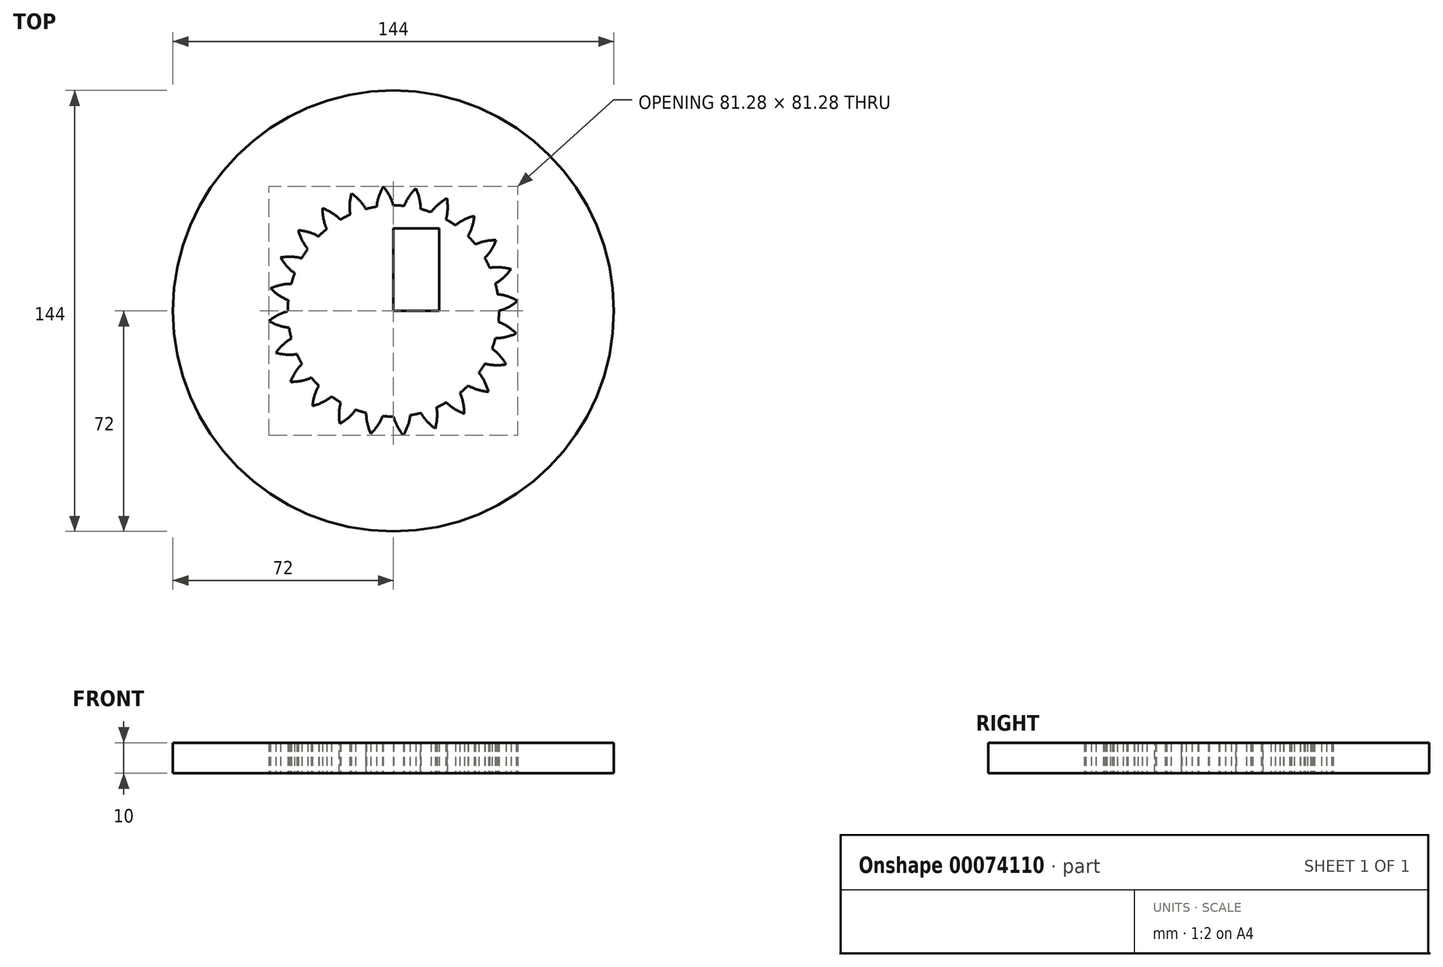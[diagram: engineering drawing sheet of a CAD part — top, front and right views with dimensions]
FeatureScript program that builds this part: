
annotation { "Feature Type Name" : "Feature", "Feature Type Description" : "" }
export const myFeature = defineFeature(function(context is Context, id is Id, definition is map)
    precondition{}
    {
        {
            assignVariable(context, id + "F0", {"name" : "T", "anyValue" : 24});
        }
        {
            var Q0;
            Q0=qCreatedBy(makeId("Top.planeOp"),FACE);
            var sketch = newSketch(context, id + "F1", { "sketchPlane" : qUnion([Q0])});
            skCircle(sketch, "E0", {"center": v(0, 0) * mm, "radius": 36 * mm, "construction": true});
            skCircle(sketch, "E1", {"center": v(0, 0) * mm, "radius": 33.83 * mm, "construction": true});
            skCircle(sketch, "E2", {"center": v(0, 0) * mm, "radius": 34.5 * mm, "construction": true});
            skCircle(sketch, "E3", {"center": v(0, 0) * mm, "radius": 41.25 * mm, "construction": true});
            skLineSegment(sketch, "E4", {"start": v(0, 0) * mm, "end": v(0, 41.25) * mm, "construction": true});
            skSolve(sketch);
        }
        {
            var Q0;
            Q0=qCreatedBy(makeId("Top.planeOp"),FACE);
            var sketch = newSketch(context, id + "F2", { "sketchPlane" : qUnion([Q0])});
            skLineSegment(sketch, "E5.1", {"start": v(0, 0) * mm, "end": v(0, 41.25) * mm, "construction": true});
            skLineSegment(sketch, "E6", {"start": v(0, 0) * mm, "end": v(0, 33.83) * mm, "construction": true});
            skLineSegment(sketch, "E7.1.0", {"start": v(0, 0) * mm, "end": v(-1.48, 33.8) * mm, "construction": true});
            skLineSegment(sketch, "E7.2.0", {"start": v(0, 0) * mm, "end": v(-2.95, 33.7) * mm, "construction": true});
            skLineSegment(sketch, "E7.3.0", {"start": v(0, 0) * mm, "end": v(-4.42, 33.54) * mm, "construction": true});
            skLineSegment(sketch, "E7.4.0", {"start": v(0, 0) * mm, "end": v(-5.87, 33.31) * mm, "construction": true});
            skLineSegment(sketch, "E7.5.0", {"start": v(0, 0) * mm, "end": v(-7.32, 33.03) * mm, "construction": true});
            skLineSegment(sketch, "E7.6.0", {"start": v(0, 0) * mm, "end": v(-8.76, 32.68) * mm, "construction": true});
            skLineSegment(sketch, "E7.7.0", {"start": v(0, 0) * mm, "end": v(-10.17, 32.26) * mm, "construction": true});
            skLineSegment(sketch, "E7.8.0", {"start": v(0, 0) * mm, "end": v(-11.57, 31.79) * mm, "construction": true});
            skLineSegment(sketch, "E7.9.0", {"start": v(0, 0) * mm, "end": v(-12.95, 31.25) * mm, "construction": true});
            skLineSegment(sketch, "E7.10.0", {"start": v(0, 0) * mm, "end": v(-14.3, 30.66) * mm, "construction": true});
            skLineSegment(sketch, "E7.11.0", {"start": v(0, 0) * mm, "end": v(-15.62, 30) * mm, "construction": true});
            skLineSegment(sketch, "E7.12.0", {"start": v(0, 0) * mm, "end": v(-16.91, 29.3) * mm, "construction": true});
            skLineSegment(sketch, "E7.13.0", {"start": v(0, 0) * mm, "end": v(-18.18, 28.53) * mm, "construction": true});
            skLineSegment(sketch, "E7.14.0", {"start": v(0, 0) * mm, "end": v(-19.4, 27.71) * mm, "construction": true});
            skLineSegment(sketch, "E7.15.0", {"start": v(0, 0) * mm, "end": v(-20.6, 26.84) * mm, "construction": true});
            skLineSegment(sketch, "E7.16.0", {"start": v(0, 0) * mm, "end": v(-21.74, 25.91) * mm, "construction": true});
            skLineSegment(sketch, "E7.17.0", {"start": v(0, 0) * mm, "end": v(-22.85, 24.94) * mm, "construction": true});
            skLineSegment(sketch, "E7.18.0", {"start": v(0, 0) * mm, "end": v(-23.92, 23.92) * mm, "construction": true});
            skLineSegment(sketch, "E7.19.0", {"start": v(0, 0) * mm, "end": v(-24.94, 22.85) * mm, "construction": true});
            skLineSegment(sketch, "E7.20.0", {"start": v(0, 0) * mm, "end": v(-25.91, 21.74) * mm, "construction": true});
            skLineSegment(sketch, "E7.21.0", {"start": v(0, 0) * mm, "end": v(-26.84, 20.6) * mm, "construction": true});
            skLineSegment(sketch, "E7.22.0", {"start": v(0, 0) * mm, "end": v(-27.71, 19.4) * mm, "construction": true});
            skLineSegment(sketch, "E7.23.0", {"start": v(0, 0) * mm, "end": v(-28.53, 18.18) * mm, "construction": true});
            skLineSegment(sketch, "E7.24.0", {"start": v(0, 0) * mm, "end": v(-29.3, 16.91) * mm, "construction": true});
            skPoint(sketch, "E7.center", {"position": v(0, 0) * mm});
            skLineSegment(sketch, "E7.anchor2", {"start": v(0, 0) * mm, "end": v(-29.3, 16.91) * mm, "construction": true});
            skLineSegment(sketch, "E8", {"start": v(-1.48, 33.8) * mm, "end": v(0, 33.86) * mm, "construction": true});
            skLineSegment(sketch, "E9", {"start": v(-2.95, 33.7) * mm, "end": v(0, 33.96) * mm, "construction": true});
            skLineSegment(sketch, "E10", {"start": v(-4.42, 33.54) * mm, "end": v(-0.03, 34.12) * mm, "construction": true});
            skLineSegment(sketch, "E11", {"start": v(-5.87, 33.31) * mm, "end": v(-0.06, 34.34) * mm, "construction": true});
            skLineSegment(sketch, "E12", {"start": v(-7.32, 33.03) * mm, "end": v(-0.12, 34.62) * mm, "construction": true});
            skLineSegment(sketch, "E13", {"start": v(-8.76, 32.68) * mm, "end": v(-0.2, 34.97) * mm, "construction": true});
            skLineSegment(sketch, "E14", {"start": v(-10.17, 32.26) * mm, "end": v(-0.32, 35.37) * mm, "construction": true});
            skLineSegment(sketch, "E15", {"start": v(-11.57, 31.79) * mm, "end": v(-0.47, 35.83) * mm, "construction": true});
            skLineSegment(sketch, "E16", {"start": v(-12.95, 31.25) * mm, "end": v(-0.67, 36.34) * mm, "construction": true});
            skLineSegment(sketch, "E17", {"start": v(-14.3, 30.66) * mm, "end": v(-0.92, 36.9) * mm, "construction": true});
            skLineSegment(sketch, "E18", {"start": v(-15.62, 30) * mm, "end": v(-1.22, 37.5) * mm, "construction": true});
            skLineSegment(sketch, "E19", {"start": v(-16.91, 29.3) * mm, "end": v(-1.57, 38.15) * mm, "construction": true});
            skLineSegment(sketch, "E20", {"start": v(-18.18, 28.53) * mm, "end": v(-2, 38.84) * mm, "construction": true});
            skLineSegment(sketch, "E21", {"start": v(-19.4, 27.71) * mm, "end": v(-2.48, 39.56) * mm, "construction": true});
            skLineSegment(sketch, "E22", {"start": v(-20.6, 26.84) * mm, "end": v(-3.03, 40.32) * mm, "construction": true});
            skLineSegment(sketch, "E23", {"start": v(-21.74, 25.91) * mm, "end": v(-3.65, 41.1) * mm, "construction": true});
            skLineSegment(sketch, "E24", {"start": v(-22.85, 24.94) * mm, "end": v(-4.35, 41.9) * mm, "construction": true});
            skLineSegment(sketch, "E25", {"start": v(-23.92, 23.92) * mm, "end": v(-5.13, 42.7) * mm, "construction": true});
            skLineSegment(sketch, "E26", {"start": v(-24.94, 22.85) * mm, "end": v(-6, 43.53) * mm, "construction": true});
            skLineSegment(sketch, "E27", {"start": v(-25.91, 21.74) * mm, "end": v(-6.94, 44.36) * mm, "construction": true});
            skLineSegment(sketch, "E28", {"start": v(-26.84, 20.6) * mm, "end": v(-7.97, 45.19) * mm, "construction": true});
            skLineSegment(sketch, "E29", {"start": v(-27.71, 19.4) * mm, "end": v(-9.09, 46) * mm, "construction": true});
            skLineSegment(sketch, "E30", {"start": v(-28.53, 18.18) * mm, "end": v(-10.29, 46.8) * mm, "construction": true});
            skLineSegment(sketch, "E31", {"start": v(-29.3, 16.91) * mm, "end": v(-11.58, 47.6) * mm, "construction": true});
            skFitSpline(sketch, "E32", {"points": [v(0, 33.83) * mm, v(0, 33.86) * mm, v(0, 33.96) * mm, v(-0.03, 34.12) * mm, v(-0.06, 34.34) * mm, v(-0.12, 34.62) * mm, v(-0.2, 34.97) * mm, v(-0.32, 35.37) * mm, v(-0.47, 35.83) * mm, v(-0.67, 36.34) * mm, v(-0.92, 36.9) * mm, v(-1.22, 37.5) * mm, v(-1.57, 38.15) * mm, v(-2, 38.84) * mm, v(-2.48, 39.56) * mm, v(-3.03, 40.32) * mm, v(-3.65, 41.1) * mm, v(-4.35, 41.9) * mm, v(-5.13, 42.7) * mm, v(-6, 43.53) * mm, v(-6.94, 44.36) * mm, v(-7.97, 45.19) * mm, v(-9.09, 46) * mm, v(-10.29, 46.8) * mm, v(-11.58, 47.6) * mm], "startDerivative": vector(-0.31, 10.71) * mm, "endDerivative": vector(-62.81, 38.1) * mm});
            skCircle(sketch, "E33.0", {"center": v(0, 0) * mm, "radius": 33.83 * mm});
            skSolve(sketch);
        }
        {
            var Q0;
            Q0=qCreatedBy(makeId("Top.planeOp"),FACE);
            var sketch = newSketch(context, id + "F3", { "sketchPlane" : qUnion([Q0])});
            skCircle(sketch, "E34.0", {"center": v(0, 0) * mm, "radius": 34.5 * mm});
            skCircle(sketch, "E34.2", {"center": v(0, 0) * mm, "radius": 36 * mm, "construction": true});
            skCircle(sketch, "E34.3", {"center": v(0, 0) * mm, "radius": 41.25 * mm});
            skLineSegment(sketch, "E34.4", {"start": v(0, 0) * mm, "end": v(0, 41.25) * mm, "construction": true});
            skCircle(sketch, "E35.0", {"center": v(0, 0) * mm, "radius": 33.83 * mm, "construction": true});
            skFitSpline(sketch, "E36.0", {"points": [v(0, 33.83) * mm, v(0, 33.86) * mm, v(0, 33.85) * mm, v(0, 33.97) * mm, v(-0.02, 34.12) * mm, v(-0.06, 34.35) * mm, v(-0.12, 34.63) * mm, v(-0.2, 34.97) * mm, v(-0.32, 35.38) * mm, v(-0.47, 35.83) * mm, v(-0.67, 36.34) * mm, v(-0.92, 36.9) * mm, v(-1.22, 37.51) * mm, v(-1.57, 38.16) * mm, v(-2, 38.85) * mm, v(-2.47, 39.57) * mm, v(-3.03, 40.33) * mm, v(-3.65, 41.1) * mm, v(-4.35, 41.9) * mm, v(-5.13, 42.72) * mm, v(-6, 43.54) * mm, v(-6.93, 44.37) * mm, v(-8, 45.21) * mm, v(-8.98, 45.95) * mm, v(-10.68, 47.06) * mm, v(-10.29, 46.8) * mm, v(-11.58, 47.6) * mm]});
            skLineSegment(sketch, "E37", {"start": v(-18.63, 69.55) * mm, "end": v(0, 0) * mm, "construction": true});
            skCircle(sketch, "E38", {"center": v(0, 0) * mm, "radius": 72 * mm});
            skLineSegment(sketch, "E39", {"start": v(-18.63, 69.55) * mm, "end": v(-8.93, 33.32) * mm});
            skLineSegment(sketch, "E40", {"start": v(0, 34.5) * mm, "end": v(0, 72) * mm});
            skLineSegment(sketch, "E41", {"start": v(0, 0) * mm, "end": v(-3.31, 41.12) * mm, "construction": true});
            skFitSpline(sketch, "E42.MirrorCS", {"points": [v(-5.41, 33.4) * mm, v(-5.42, 33.42) * mm, v(-5.42, 33.4) * mm, v(-5.43, 33.54) * mm, v(-5.44, 33.68) * mm, v(-5.44, 33.91) * mm, v(-5.43, 34.2) * mm, v(-5.4, 34.56) * mm, v(-5.35, 34.97) * mm, v(-5.27, 35.45) * mm, v(-5.15, 35.98) * mm, v(-5, 36.58) * mm, v(-4.8, 37.22) * mm, v(-4.55, 37.92) * mm, v(-4.25, 38.67) * mm, v(-3.9, 39.46) * mm, v(-3.47, 40.29) * mm, v(-2.97, 41.16) * mm, v(-2.4, 42.06) * mm, v(-1.77, 42.99) * mm, v(-1.05, 43.94) * mm, v(-0.26, 44.9) * mm, v(0.65, 45.9) * mm, v(1.51, 46.8) * mm, v(3, 48.16) * mm, v(2.67, 47.85) * mm, v(3.82, 48.83) * mm]});
            skLineSegment(sketch, "E43", {"start": v(-0.54, 36) * mm, "end": v(0, 0) * mm, "construction": true});
            skSolve(sketch);
        }
        {
            var Q0;
            {var subQ7=sQuery(id+"F3.wireOp",EDGE,"E34.3");var subQ9=makeQuery(id+"F3.imprint","INTERSECT",VERTEX,{"derivedFrom":[subQ7,sQuery(id+"F3.wireOp",EDGE,"E36.0")]});Q0=makeQuery(id+"F3.imprint","IMPRINT",FACE,{"disambiguationData":[TD([[makeQuery(id+"F3.imprint","IMPRINT",EDGE,{"disambiguationData":[TD([[subQ9,1.0]])],"derivedFrom":subQ7}),-1.0]])]});}
            var Q1;
            {var subQ0=sQuery(id+"F3.wireOp",EDGE,"E42.MirrorCS");var subQ1=sQuery(id+"F3.wireOp",EDGE,"E34.3");var subQ2=makeQuery(id+"F3.imprint","INTERSECT",VERTEX,{"derivedFrom":[subQ1,subQ0]});Q1=makeQuery(id+"F3.imprint","IMPRINT",FACE,{"disambiguationData":[TD([[makeQuery(id+"F3.imprint","IMPRINT",EDGE,{"disambiguationData":[TD([[subQ2,1.0]])],"derivedFrom":subQ1}),-1.0]])]});}
            var Q2;
            {var subQ0=sQuery(id+"F3.wireOp",EDGE,"E40");var subQ1=sQuery(id+"F3.wireOp",EDGE,"E34.0");var subQ2=makeQuery(id+"F3.imprint","INTERSECT",VERTEX,{"derivedFrom":[subQ1,subQ0]});Q2=makeQuery(id+"F3.imprint","IMPRINT",FACE,{"disambiguationData":[TD([[makeQuery(id+"F3.imprint","IMPRINT",EDGE,{"disambiguationData":[TD([[subQ2,-1.0]])],"derivedFrom":subQ1}),-1.0]])]});}
            var Q3;
            {var subQ0=sQuery(id+"F3.wireOp",EDGE,"E39");var subQ1=sQuery(id+"F3.wireOp",EDGE,"E34.0");var subQ2=makeQuery(id+"F3.imprint","INTERSECT",VERTEX,{"derivedFrom":[subQ1,subQ0]});Q3=makeQuery(id+"F3.imprint","IMPRINT",FACE,{"disambiguationData":[TD([[makeQuery(id+"F3.imprint","IMPRINT",EDGE,{"disambiguationData":[TD([[subQ2,1.0]])],"derivedFrom":subQ1}),-1.0]])]});}
            var Q4;
            {var subQ0=sQuery(id+"F3.wireOp",EDGE,"E36.0");var subQ1=sQuery(id+"F3.wireOp",EDGE,"E34.3");var subQ2=makeQuery(id+"F3.imprint","INTERSECT",VERTEX,{"derivedFrom":[subQ1,subQ0]});Q4=makeQuery(id+"F3.imprint","IMPRINT",FACE,{"disambiguationData":[TD([[makeQuery(id+"F3.imprint","IMPRINT",EDGE,{"disambiguationData":[TD([[subQ2,1.0]])],"derivedFrom":subQ1}),1.0]])]});}
            var Q5;
            {var subQ0=sQuery(id+"F3.wireOp",EDGE,"KCeHU3UQ-lOB1-B6P4-Ijrd-39XFGKG8JNLL");Q5=makeQuery(id+"F3.imprint","IMPRINT",FACE,{"disambiguationData":[TD([[makeQuery(id+"F3.imprint","IMPRINT",EDGE,{"derivedFrom":subQ0}),1.0]])]});}
            var Q6;
            {var subQ0=sQuery(id+"F3.wireOp",EDGE,"MMJC9PiU-g5KQ-n5en-Otxz-z1taWbiqTUHW");Q6=makeQuery(id+"F3.imprint","IMPRINT",FACE,{"disambiguationData":[TD([[makeQuery(id+"F3.imprint","IMPRINT",EDGE,{"derivedFrom":subQ0}),-1.0]])]});}
            var Q7;
            {var subQ3=sQuery(id+"F3.wireOp",EDGE,"E42.MirrorCS");var subQ7=sQuery(id+"F3.wireOp",EDGE,"E34.3");var subQ9=makeQuery(id+"F3.imprint","INTERSECT",VERTEX,{"derivedFrom":[subQ7,subQ3]});Q7=makeQuery(id+"F3.imprint","IMPRINT",FACE,{"disambiguationData":[TD([[makeQuery(id+"F3.imprint","IMPRINT",EDGE,{"disambiguationData":[TD([[subQ9,-1.0]])],"derivedFrom":subQ7}),-1.0]])]});}
            extrude(context, id + "F4", {"entities" : qUnion([Q0, Q1, Q2, Q3, Q4, Q5, Q6, Q7]), "depth" : 10 * mm});
        }
        {
            var Q0;
            Q0=qCreatedBy(makeId("Front.planeOp"),FACE);
            var sketch = newSketch(context, id + "F5", { "sketchPlane" : qUnion([Q0])});
            skLineSegment(sketch, "E44", {"start": v(0, 0) * mm, "end": v(0, 40) * mm});
            skSolve(sketch);
        }
        {
            var Q0;
            Q0=makeQuery(id+"F4.opExtrude","SWEPT_BODY",BODY,{"disambiguationData":[OSD([sQuery(id+"F3.wireOp",EDGE,"E34.0"),sQuery(id+"F3.wireOp",EDGE,"E36.0"),sQuery(id+"F3.wireOp",EDGE,"50ee4050-3f94-4cd3-8dc1-42a7f2aab2de0.MirrorCS"),sQuery(id+"F3.wireOp",EDGE,"E38"),sQuery(id+"F3.wireOp",EDGE,"E39"),sQuery(id+"F3.wireOp",EDGE,"E40")])]});
            var Q1;
            Q1=sQuery(id+"F5.wireOp",EDGE,"E44");
            circularPattern(context, id + "F6", {"operationType" : NewBodyOperationType.ADD, "entities" : qUnion([Q0]), "axis" : qUnion([Q1]), "angle" : 360 * degree, "instanceCount" : getVariable(context, 'T'), "equalSpace" : true});
        }
        {
            var Q0;
            Q0=qCreatedBy(makeId("Top.planeOp"),FACE);
            var sketch = newSketch(context, id + "F7", { "sketchPlane" : qUnion([Q0])});
            skLineSegment(sketch, "E45", {"start": v(0, 0) * mm, "end": v(15, 0) * mm});
            skLineSegment(sketch, "E46", {"start": v(15, 0) * mm, "end": v(15, 27) * mm});
            skLineSegment(sketch, "E47", {"start": v(15, 27) * mm, "end": v(0, 27) * mm});
            skLineSegment(sketch, "E48", {"start": v(0, 27) * mm, "end": v(0, 0) * mm});
            skSolve(sketch);
        }
        {
            var Q0;
            Q0=makeQuery(id+"F7.imprint","IMPRINT",FACE,{"disambiguationData":[TD([[makeQuery(id+"F7.imprint","IMPRINT",EDGE,{"derivedFrom":sQuery(id+"F7.wireOp",EDGE,"E45")}),1.0]])]});
            extrude(context, id + "F8", {"entities" : qUnion([Q0]), "depth" : 10 * mm});
        }
    });
